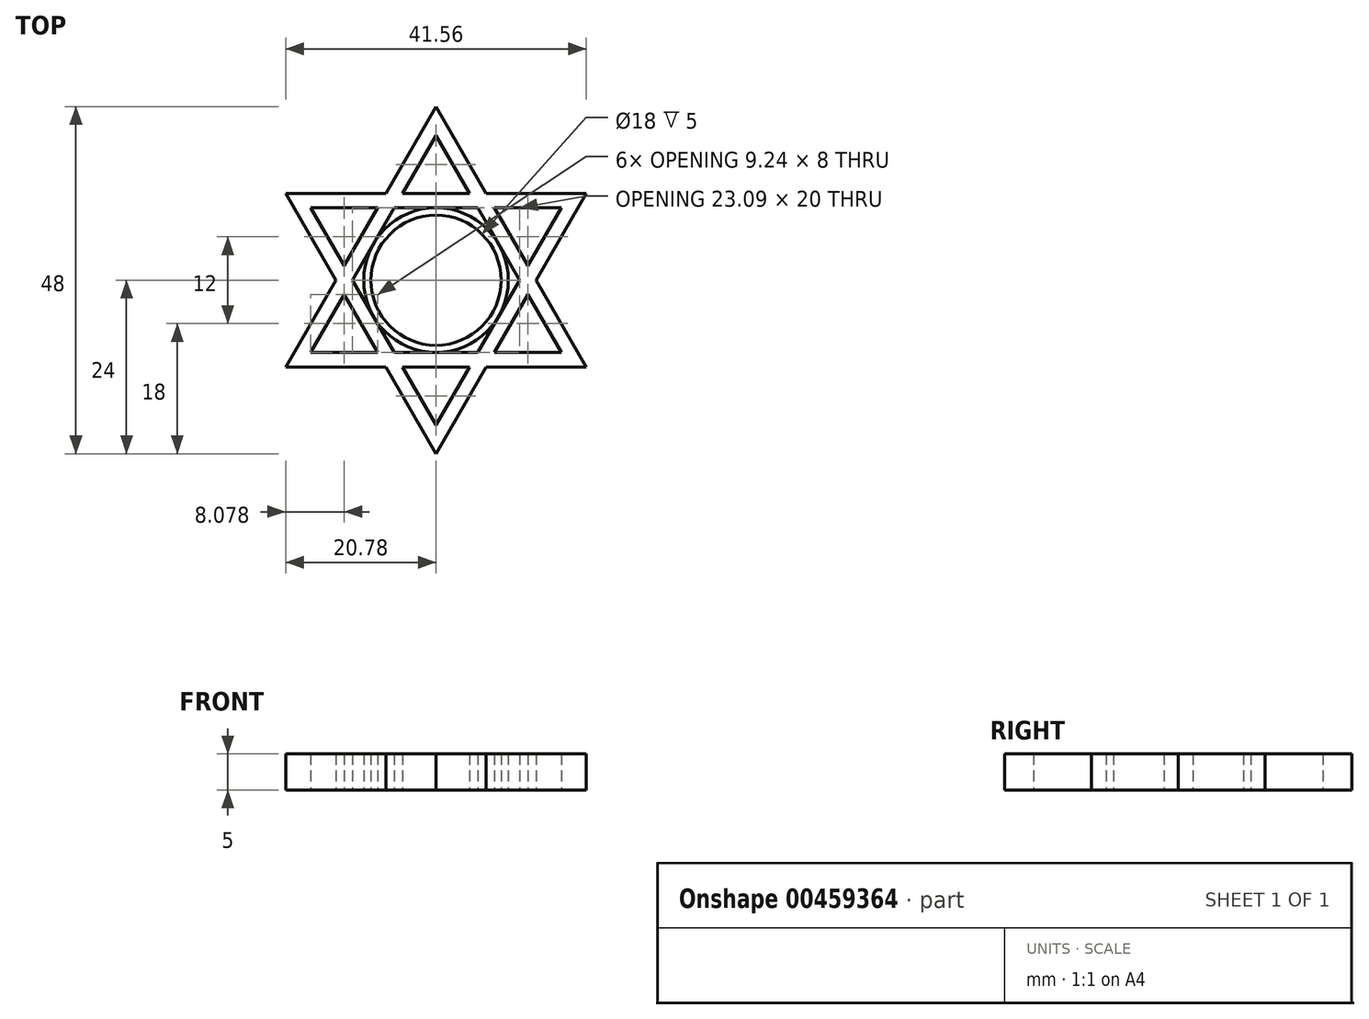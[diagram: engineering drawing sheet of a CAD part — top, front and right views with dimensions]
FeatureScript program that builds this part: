
annotation { "Feature Type Name" : "Feature", "Feature Type Description" : "" }
export const myFeature = defineFeature(function(context is Context, id is Id, definition is map)
    precondition{}
    {
        {
            var Q0;
            Q0=qCreatedBy(makeId("Top.planeOp"),FACE);
            var sketch = newSketch(context, id + "F0", { "sketchPlane" : qUnion([Q0])});
            skCircle(sketch, "E0", {"center": v(0, 0) * mm, "radius": 10 * mm});
            skLineSegment(sketch, "E1", {"start": v(0, 10) * mm, "end": v(17.32, 10) * mm});
            skLineSegment(sketch, "E2", {"start": v(0, 10) * mm, "end": v(-17.32, 10) * mm});
            skLineSegment(sketch, "E3", {"start": v(-17.32, 10) * mm, "end": v(0, -20) * mm});
            skLineSegment(sketch, "E4", {"start": v(0, -20) * mm, "end": v(17.32, 10) * mm});
            skLineSegment(sketch, "E5", {"start": v(0, -10) * mm, "end": v(-17.32, -10) * mm});
            skLineSegment(sketch, "E6", {"start": v(0, -10) * mm, "end": v(17.32, -10) * mm});
            skLineSegment(sketch, "E7", {"start": v(17.32, -10) * mm, "end": v(0, 20) * mm});
            skLineSegment(sketch, "E8", {"start": v(0, 20) * mm, "end": v(-17.32, -10) * mm});
            skCircle(sketch, "E9", {"center": v(0, 0) * mm, "radius": 9 * mm});
            skLineSegment(sketch, "E10", {"start": v(0, 20) * mm, "end": v(0, 24) * mm});
            skLineSegment(sketch, "E11", {"start": v(-19.05, -9) * mm, "end": v(0, 24) * mm});
            skLineSegment(sketch, "E12", {"start": v(19.05, -9) * mm, "end": v(0, 24) * mm});
            skLineSegment(sketch, "E13", {"start": v(-10.97, -12) * mm, "end": v(20.78, -12) * mm});
            skLineSegment(sketch, "E14", {"start": v(-10.97, -12) * mm, "end": v(-20.78, -12) * mm});
            skLineSegment(sketch, "E15", {"start": v(-19.05, -9) * mm, "end": v(-20.78, -12) * mm});
            skLineSegment(sketch, "E16", {"start": v(19.05, -9) * mm, "end": v(20.78, -12) * mm});
            skLineSegment(sketch, "E17", {"start": v(-14.92, 12) * mm, "end": v(20.78, 12) * mm});
            skLineSegment(sketch, "E18", {"start": v(-14.92, 12) * mm, "end": v(-20.78, 12) * mm});
            skLineSegment(sketch, "E19", {"start": v(16.82, 5.14) * mm, "end": v(20.78, 12) * mm});
            skLineSegment(sketch, "E20", {"start": v(16.82, 5.14) * mm, "end": v(0, -24) * mm});
            skLineSegment(sketch, "E21", {"start": v(-17.66, 6.58) * mm, "end": v(-20.78, 12) * mm});
            skLineSegment(sketch, "E22", {"start": v(-17.66, 6.58) * mm, "end": v(0, -24) * mm});
            skSolve(sketch);
        }
        {
            var Q0;
            Q0 = qSketchRegion(id + "F0", true);
            var Q1;
            {var subQ0=sQuery(id+"F0.wireOp",EDGE,"E7");var subQ2=sQuery(id+"F0.wireOp",EDGE,"E1");var subQ3=makeQuery(id+"F0.imprint","INTERSECT",VERTEX,{"derivedFrom":[subQ2,subQ0]});Q1=makeQuery(id+"F0.imprint","IMPRINT",FACE,{"disambiguationData":[TD([[makeQuery(id+"F0.imprint","IMPRINT",EDGE,{"disambiguationData":[TD([[subQ3,-1.0]])],"derivedFrom":subQ2}),-1.0]])]});}
            var Q2;
            {var subQ0=sQuery(id+"F0.wireOp",EDGE,"E8");var subQ4=sQuery(id+"F0.wireOp",EDGE,"E2");var subQ5=makeQuery(id+"F0.imprint","INTERSECT",VERTEX,{"derivedFrom":[subQ4,subQ0]});Q2=makeQuery(id+"F0.imprint","IMPRINT",FACE,{"disambiguationData":[TD([[makeQuery(id+"F0.imprint","IMPRINT",EDGE,{"disambiguationData":[TD([[subQ5,-1.0]])],"derivedFrom":subQ4}),1.0]])]});}
            var Q3;
            {var subQ1=sQuery(id+"F0.wireOp",EDGE,"E3");var subQ8=makeQuery(id+"F0.imprint","INTERSECT",VERTEX,{"derivedFrom":[sQuery(id+"F0.wireOp",EDGE,"E0"),subQ1]});Q3=makeQuery(id+"F0.imprint","IMPRINT",FACE,{"disambiguationData":[TD([[makeQuery(id+"F0.imprint","IMPRINT",EDGE,{"disambiguationData":[TD([[subQ8,1.0]])],"derivedFrom":subQ1}),-1.0]])]});}
            var Q4;
            {var subQ1=sQuery(id+"F0.wireOp",EDGE,"E4");var subQ8=makeQuery(id+"F0.imprint","INTERSECT",VERTEX,{"derivedFrom":[sQuery(id+"F0.wireOp",EDGE,"E0"),subQ1]});Q4=makeQuery(id+"F0.imprint","IMPRINT",FACE,{"disambiguationData":[TD([[makeQuery(id+"F0.imprint","IMPRINT",EDGE,{"disambiguationData":[TD([[subQ8,1.0]])],"derivedFrom":subQ1}),-1.0]])]});}
            var Q5;
            {var subQ1=sQuery(id+"F0.wireOp",EDGE,"E5");var subQ5=sQuery(id+"F0.wireOp",EDGE,"E3");var subQ6=makeQuery(id+"F0.imprint","INTERSECT",VERTEX,{"derivedFrom":[subQ5,subQ1]});Q5=makeQuery(id+"F0.imprint","IMPRINT",FACE,{"disambiguationData":[TD([[makeQuery(id+"F0.imprint","IMPRINT",EDGE,{"disambiguationData":[TD([[subQ6,-1.0]])],"derivedFrom":subQ5}),1.0]])]});}
            var Q6;
            Q6=makeQuery(id+"F0.imprint","IMPRINT",FACE,{"disambiguationData":[TD([[makeQuery(id+"F0.imprint","IMPRINT",EDGE,{"derivedFrom":sQuery(id+"F0.wireOp",EDGE,"E9")}),-1.0]])]});
            var Q7;
            {var subQ5=sQuery(id+"F0.wireOp",EDGE,"E7");var subQ6=sQuery(id+"F0.wireOp",EDGE,"E1");var subQ7=makeQuery(id+"F0.imprint","INTERSECT",VERTEX,{"derivedFrom":[subQ6,subQ5]});Q7=makeQuery(id+"F0.imprint","IMPRINT",FACE,{"disambiguationData":[TD([[makeQuery(id+"F0.imprint","IMPRINT",EDGE,{"disambiguationData":[TD([[subQ7,-1.0]])],"derivedFrom":subQ5}),1.0]])]});}
            extrude(context, id + "F1", {"entities" : qUnion([Q0, Q1, Q2, Q3, Q4, Q5, Q6, Q7]), "depth" : 5 * mm, "offsetDistance" : 25 * mm});
        }
    });
